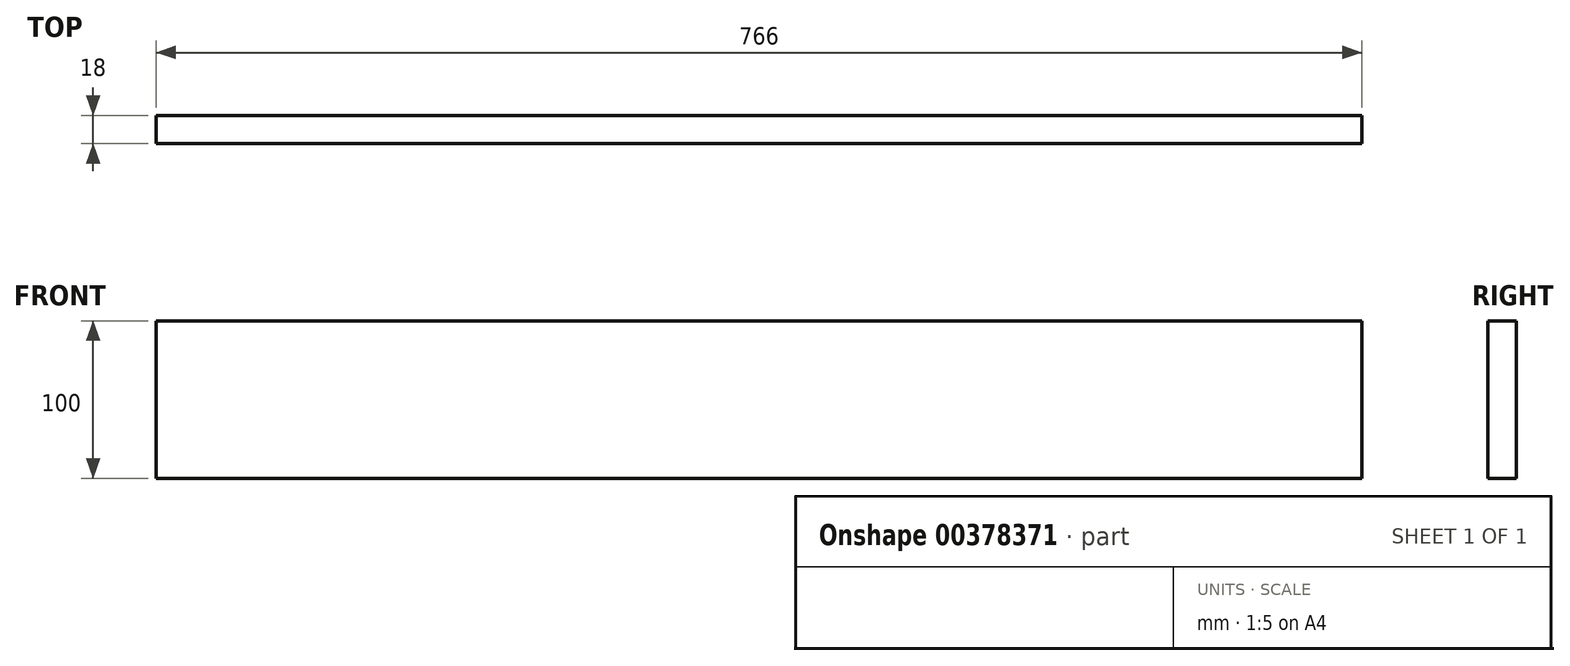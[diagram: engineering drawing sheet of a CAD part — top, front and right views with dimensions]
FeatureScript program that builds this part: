
annotation { "Feature Type Name" : "Feature", "Feature Type Description" : "" }
export const myFeature = defineFeature(function(context is Context, id is Id, definition is map)
    precondition{}
    {
        {
            var Q0;
            Q0=qCreatedBy(makeId("Right.planeOp"),FACE);
            var sketch = newSketch(context, id + "F0", { "sketchPlane" : qUnion([Q0])});
            skLineSegment(sketch, "E0.bottom", {"start": v(9, 50) * mm, "end": v(-9, 50) * mm});
            skLineSegment(sketch, "E0.top", {"start": v(9, -50) * mm, "end": v(-9, -50) * mm});
            skLineSegment(sketch, "E0.left", {"start": v(9, 50) * mm, "end": v(9, -50) * mm});
            skLineSegment(sketch, "E0.right", {"start": v(-9, 50) * mm, "end": v(-9, -50) * mm});
            skPoint(sketch, "E0.middle", {"position": v(0, 0) * mm});
            skSolve(sketch);
        }
        {
            var Q0;
            Q0=qSketchRegion(id+"F0",true);
            extrude(context, id + "F1", {"entities" : qUnion([Q0]), "depth" : 766 * mm});
        }
    });
